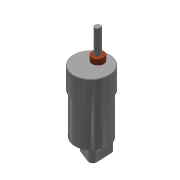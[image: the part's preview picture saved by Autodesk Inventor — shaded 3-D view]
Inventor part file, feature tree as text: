
AUTODESK INVENTOR PART (.ipt)
format: ipt  version: 2013 (Build 170138000, 138)  size: 220,160 bytes
history: native  units: in
note: dims shown in document units (in); Inventor stores cm internally (conversion verified against a paired STEP export)
features: other x4, sketch x4
ambient origin geometry x8: Origin, YZ Plane, XZ Plane, XY Plane, X Axis, Y Axis, Z Axis, Center Point
bodies: Solid1 (feature_tree), Solid2 (feature_tree)
feature tree (8):
  other  "Tetrix motor.ipt"
  other  "DC_MOTOR_2011::Tetrix motor.ipt"
  other  "Solid2::Tetrix motor.ipt"
  other  "TaggingFeature1"
  sketch  "Sketch1"  dims[d0=0.3937in]
  sketch  "Sketch2"  dims[d1=0.5909in d3=0.3436in d5=0.4528in d6=0.4528in d7=0.1654in d8=0.0in d9=0.748in d11=0.4331in d12=0.3661in d13=0.0in d14=0.2165in d16=0.0472in d17=0.0in d18=0.0197in d19=0.0787in d20=0.1181in d21=0.1181in d22=0.5906in d23=0.0in]
  sketch  "Sketch3"
  sketch  "Sketch4"
